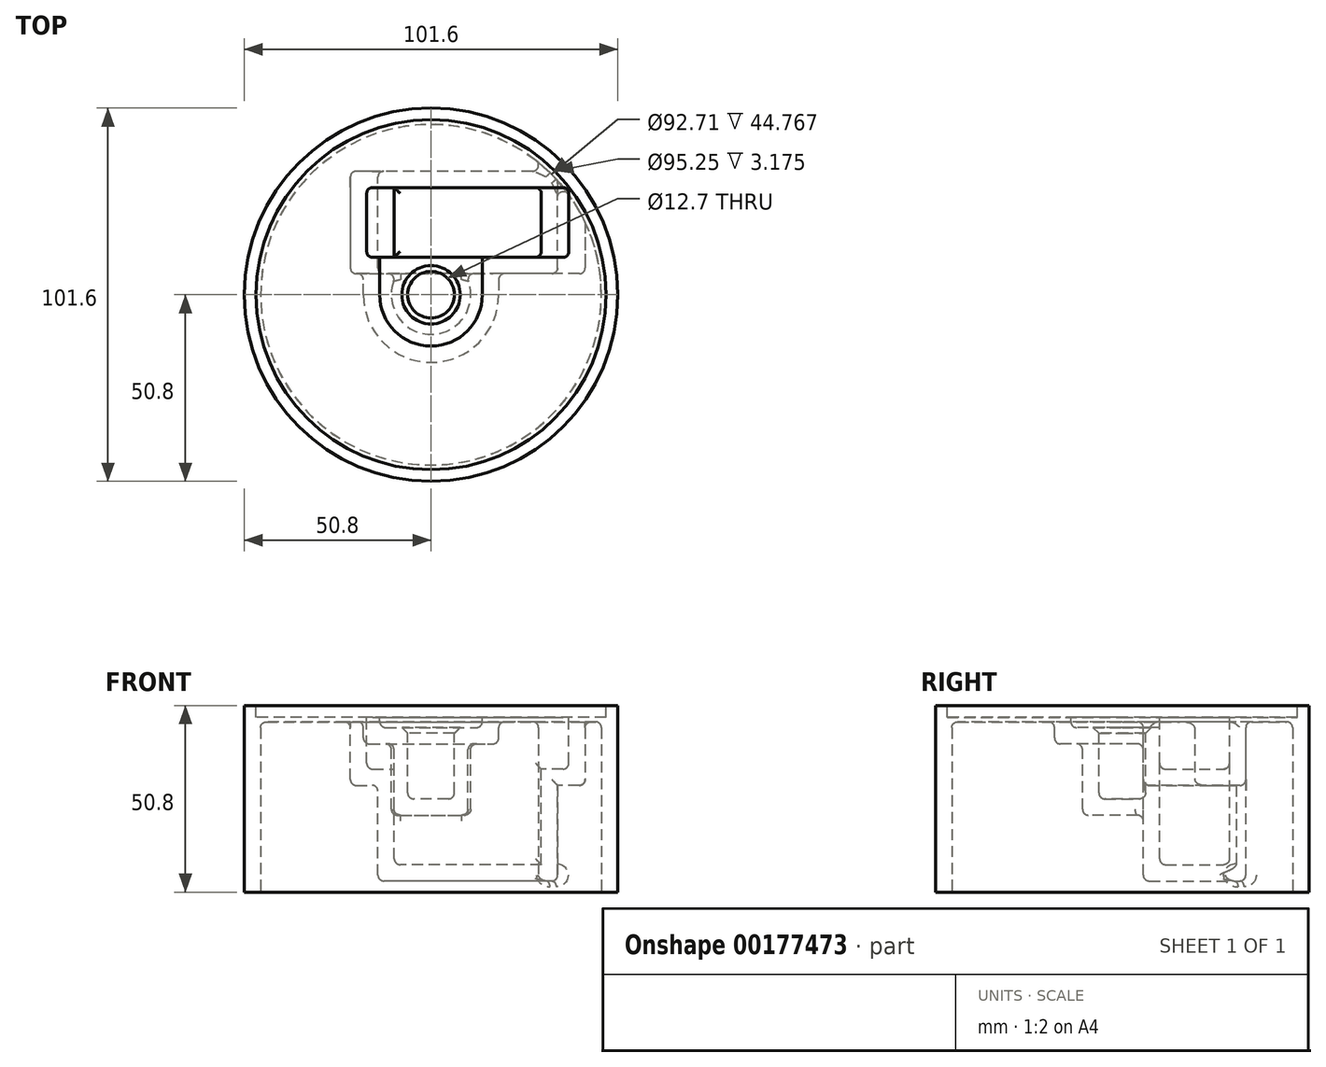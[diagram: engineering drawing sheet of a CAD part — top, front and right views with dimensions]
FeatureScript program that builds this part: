
annotation { "Feature Type Name" : "Feature", "Feature Type Description" : "" }
export const myFeature = defineFeature(function(context is Context, id is Id, definition is map)
    precondition{}
    {
        {
            var Q0;
            Q0=qCreatedBy(makeId("Top.planeOp"),FACE);
            var sketch = newSketch(context, id + "F0", { "sketchPlane" : qUnion([Q0])});
            skCircle(sketch, "E0", {"center": v(0, 0) * mm, "radius": 50.8 * mm});
            skSolve(sketch);
        }
        {
            var Q0;
            Q0 = qSketchRegion(id + "F0", true);
            extrude(context, id + "F1", {"entities" : qUnion([Q0]), "depth" : 50.8 * mm});
        }
        {
            var Q0;
            Q0=makeQuery(id+"F1.opExtrude","CAP_FACE",FACE,{"disambiguationData":[OSD([sQuery(id+"F0.wireOp",EDGE,"E0")])],"isStart":false});
            var sketch = newSketch(context, id + "F2", { "sketchPlane" : qUnion([Q0])});
            skCircle(sketch, "E1", {"center": v(0, 0) * mm, "radius": 13.02 * mm});
            skCircle(sketch, "E2", {"center": v(0, 19.69) * mm, "radius": 6.67 * mm});
            skLineSegment(sketch, "E3", {"start": v(-24.88, 13.98) * mm, "end": v(-19.78, -16.5) * mm});
            skLineSegment(sketch, "E4", {"start": v(-19.78, -16.5) * mm, "end": v(3.2, -22.09) * mm});
            skLineSegment(sketch, "E5", {"start": v(3.2, -22.09) * mm, "end": v(-19.1, -28.35) * mm});
            skLineSegment(sketch, "E6", {"start": v(-19.1, -28.35) * mm, "end": v(-34.98, -6.69) * mm});
            skLineSegment(sketch, "E7", {"start": v(-34.98, -6.69) * mm, "end": v(-24.88, 13.98) * mm});
            skSolve(sketch);
        }
        {
            var Q0;
            Q0=makeQuery(id+"F2.imprint","IMPRINT",FACE,{"disambiguationData":[TD([[makeQuery(id+"F2.imprint","IMPRINT",EDGE,{"derivedFrom":sQuery(id+"F2.wireOp",EDGE,"E1")}),-1.0]])]});
            var sketch = newSketch(context, id + "F3", { "sketchPlane" : qUnion([Q0])});
            skLineSegment(sketch, "E8.bottom", {"start": v(30, 10.19) * mm, "end": v(-10, 10.18) * mm});
            skLineSegment(sketch, "E8.top", {"start": v(30, 29.19) * mm, "end": v(-10, 29.18) * mm});
            skLineSegment(sketch, "E8.left", {"start": v(30, 10.19) * mm, "end": v(30, 29.19) * mm});
            skLineSegment(sketch, "E8.right", {"start": v(-10, 10.18) * mm, "end": v(-10, 29.18) * mm});
            skPoint(sketch, "E8.middle", {"position": v(10, 19.69) * mm});
            skSolve(sketch);
        }
        {
            var Q0;
            Q0 = qSketchRegion(id + "F3", true);
            extrude(context, id + "F4", {"entities" : qUnion([Q0]), "operationType" : NewBodyOperationType.REMOVE, "oppositeDirection" : true, "depth" : 43.3 * mm});
        }
        {
            var Q0;
            Q0=makeQuery(id+"F2.imprint","IMPRINT",FACE,{"disambiguationData":[TD([[makeQuery(id+"F2.imprint","IMPRINT",EDGE,{"derivedFrom":sQuery(id+"F2.wireOp",EDGE,"E1")}),-1.0]])]});
            var sketch = newSketch(context, id + "F5", { "sketchPlane" : qUnion([Q0])});
            skLineSegment(sketch, "E9.0", {"start": v(-10, 10.18) * mm, "end": v(-10, 29.18) * mm});
            skLineSegment(sketch, "E9.1", {"start": v(30, 10.19) * mm, "end": v(30, 29.19) * mm});
            skLineSegment(sketch, "E10", {"start": v(-10, 29.18) * mm, "end": v(-17.5, 29.18) * mm});
            skLineSegment(sketch, "E11", {"start": v(-17.5, 29.18) * mm, "end": v(-17.5, 10.18) * mm});
            skLineSegment(sketch, "E12", {"start": v(-17.5, 10.18) * mm, "end": v(-10, 10.18) * mm});
            skLineSegment(sketch, "E13", {"start": v(30, 29.18) * mm, "end": v(37.5, 29.18) * mm});
            skLineSegment(sketch, "E14", {"start": v(37.5, 29.19) * mm, "end": v(37.5, 10.18) * mm});
            skLineSegment(sketch, "E15", {"start": v(37.5, 10.18) * mm, "end": v(30, 10.18) * mm});
            skSolve(sketch);
        }
        {
            var Q0;
            Q0 = qSketchRegion(id + "F5", true);
            extrude(context, id + "F6", {"entities" : qUnion([Q0]), "operationType" : NewBodyOperationType.REMOVE, "oppositeDirection" : true, "depth" : (43.3 - 26) * mm});
        }
        {
            var Q0;
            Q0=makeQuery(id+"F2.imprint","IMPRINT",FACE,{"disambiguationData":[TD([[makeQuery(id+"F2.imprint","IMPRINT",EDGE,{"derivedFrom":sQuery(id+"F2.wireOp",EDGE,"E1")}),-1.0]])]});
            var sketch = newSketch(context, id + "F7", { "sketchPlane" : qUnion([Q0])});
            skArc(sketch, "E16", {"start": v(-13.97, 0) * mm, "mid": v(0, -13.97) * mm, "end": v(13.97, 0) * mm});
            skLineSegment(sketch, "E17", {"start": v(-13.97, 0) * mm, "end": v(-13.97, 10.18) * mm});
            skLineSegment(sketch, "E18", {"start": v(-13.97, 10.18) * mm, "end": v(13.97, 10.18) * mm});
            skLineSegment(sketch, "E19", {"start": v(13.97, 10.18) * mm, "end": v(13.97, 0) * mm});
            skSolve(sketch);
        }
        {
            var Q0;
            Q0 = qSketchRegion(id + "F7", true);
            var Q1;
            Q1=makeQuery(id+"F6.boolean.opBoolean","COPY",FACE,{"derivedFrom":makeQuery(id+"F6.opExtrude","CAP_FACE",FACE,{"disambiguationData":[OSD([sQuery(id+"F5.wireOp",EDGE,"E9.0"),sQuery(id+"F5.wireOp",EDGE,"E10"),sQuery(id+"F5.wireOp",EDGE,"E11"),sQuery(id+"F5.wireOp",EDGE,"E12")])],"isStart":false})});
            extrude(context, id + "F8", {"entities" : qUnion([Q0]), "operationType" : NewBodyOperationType.REMOVE, "oppositeDirection" : true, "endBoundEntityFace" : qUnion([Q1]), "depth" : 6 * mm});
        }
        {
            var Q0;
            Q0=makeQuery(id+"F2.imprint","IMPRINT",FACE,{"disambiguationData":[TD([[makeQuery(id+"F2.imprint","IMPRINT",EDGE,{"derivedFrom":sQuery(id+"F2.wireOp",EDGE,"E1")}),1.0]])]});
            var sketch = newSketch(context, id + "F9", { "sketchPlane" : qUnion([Q0])});
            skCircle(sketch, "E20", {"center": v(0, 0) * mm, "radius": 6.35 * mm});
            skSolve(sketch);
        }
        {
            var Q0;
            Q0 = qSketchRegion(id + "F9", true);
            extrude(context, id + "F10", {"entities" : qUnion([Q0]), "operationType" : NewBodyOperationType.REMOVE, "oppositeDirection" : true, "depth" : 25.4 * mm});
        }
        {
            var Q0;
            Q0=makeQuery(id+"F1.opExtrude","CAP_FACE",FACE,{"disambiguationData":[OSD([sQuery(id+"F0.wireOp",EDGE,"E0")])],"isStart":true});
            shell(context, id + "F11", {"entities" : qUnion([Q0]), "thickness" : 4.44 * mm});
        }
        {
            var Q0;
            Q0=makeQuery(id+"F2.imprint","IMPRINT",FACE,{"disambiguationData":[TD([[makeQuery(id+"F2.imprint","IMPRINT",EDGE,{"derivedFrom":sQuery(id+"F2.wireOp",EDGE,"E1")}),-1.0]])]});
            var sketch = newSketch(context, id + "F12", { "sketchPlane" : qUnion([Q0])});
            skCircle(sketch, "E21", {"center": v(0, 0) * mm, "radius": 47.62 * mm});
            skSolve(sketch);
        }
        {
            var Q0;
            Q0 = qSketchRegion(id + "F12", true);
            extrude(context, id + "F13", {"entities" : qUnion([Q0]), "operationType" : NewBodyOperationType.REMOVE, "oppositeDirection" : true, "depth" : 3.17 * mm});
        }
        {
            var Q0;
            Q0=makeQuery(id+"F8.boolean.opBoolean","COPY",EDGE,{"derivedFrom":makeQuery(id+"F8.opExtrude","CAP_EDGE",EDGE,{"disambiguationData":[OSD([sQuery(id+"F7.wireOp",EDGE,"E17")])],"isStart":false})});
            var Q1;
            Q1=makeQuery(id+"F6.boolean.opBoolean","COPY",EDGE,{"derivedFrom":makeQuery(id+"F6.opExtrude","CAP_EDGE",EDGE,{"disambiguationData":[OSD([sQuery(id+"F5.wireOp",EDGE,"E11")])],"isStart":false})});
            var Q2;
            Q2=makeQuery(id+"F6.boolean.opBoolean","COPY",EDGE,{"derivedFrom":makeQuery(id+"F6.opExtrude","CAP_EDGE",EDGE,{"disambiguationData":[OSD([sQuery(id+"F5.wireOp",EDGE,"E10")])],"isStart":false})});
            var Q3;
            Q3=makeQuery(id+"F6.boolean.opBoolean","COPY",EDGE,{"derivedFrom":makeQuery(id+"F6.opExtrude","CAP_EDGE",EDGE,{"disambiguationData":[OSD([sQuery(id+"F5.wireOp",EDGE,"E9.0")])],"isStart":false})});
            var Q4;
            Q4=makeQuery(id+"F4.boolean.opBoolean","COPY",EDGE,{"derivedFrom":makeQuery(id+"F4.opExtrude","CAP_EDGE",EDGE,{"disambiguationData":[OSD([sQuery(id+"F3.wireOp",EDGE,"E8.right")])],"isStart":false})});
            var Q5;
            Q5=makeQuery(id+"F4.boolean.opBoolean","COPY",EDGE,{"derivedFrom":makeQuery(id+"F4.opExtrude","CAP_EDGE",EDGE,{"disambiguationData":[OSD([sQuery(id+"F3.wireOp",EDGE,"E8.top")])],"isStart":false})});
            var Q6;
            Q6=makeQuery(id+"F6.boolean.opBoolean","COPY",EDGE,{"derivedFrom":makeQuery(id+"F6.opExtrude","SWEPT_EDGE",EDGE,{"disambiguationData":[OSD([sQuery(id+"F5.wireOp",EDGE,"E11"),sQuery(id+"F5.wireOp",EDGE,"E12")])]})});
            var Q7;
            Q7=makeQuery(id+"F6.boolean.opBoolean","COPY",EDGE,{"derivedFrom":makeQuery(id+"F6.opExtrude","CAP_EDGE",EDGE,{"disambiguationData":[OSD([sQuery(id+"F5.wireOp",EDGE,"E12")])],"isStart":false})});
            var Q8;
            Q8=makeQuery(id+"F4.boolean.opBoolean","COPY",EDGE,{"derivedFrom":makeQuery(id+"F4.opExtrude","CAP_EDGE",EDGE,{"disambiguationData":[OSD([sQuery(id+"F3.wireOp",EDGE,"E8.bottom")])],"isStart":false})});
            var Q9;
            Q9=makeQuery(id+"F4.boolean.opBoolean","COPY",EDGE,{"derivedFrom":makeQuery(id+"F4.opExtrude","SWEPT_EDGE",EDGE,{"disambiguationData":[OSD([sQuery(id+"F3.wireOp",EDGE,"E8.bottom"),sQuery(id+"F3.wireOp",EDGE,"E8.left")])]})});
            var Q10;
            Q10=makeQuery(id+"F4.boolean.opBoolean","COPY",EDGE,{"derivedFrom":makeQuery(id+"F4.opExtrude","SWEPT_EDGE",EDGE,{"disambiguationData":[OSD([sQuery(id+"F3.wireOp",EDGE,"E8.top"),sQuery(id+"F3.wireOp",EDGE,"E8.left")])]})});
            var Q11;
            Q11=makeQuery(id+"F6.boolean.opBoolean","COPY",EDGE,{"derivedFrom":makeQuery(id+"F6.opExtrude","CAP_EDGE",EDGE,{"disambiguationData":[OSD([sQuery(id+"F5.wireOp",EDGE,"E13")])],"isStart":false})});
            var Q12;
            Q12=makeQuery(id+"F6.boolean.opBoolean","COPY",EDGE,{"derivedFrom":makeQuery(id+"F6.opExtrude","SWEPT_EDGE",EDGE,{"disambiguationData":[OSD([sQuery(id+"F5.wireOp",EDGE,"E13"),sQuery(id+"F5.wireOp",EDGE,"E14")])]})});
            var Q13;
            Q13=makeQuery(id+"F6.boolean.opBoolean","COPY",EDGE,{"derivedFrom":makeQuery(id+"F6.opExtrude","SWEPT_EDGE",EDGE,{"disambiguationData":[OSD([sQuery(id+"F5.wireOp",EDGE,"E14"),sQuery(id+"F5.wireOp",EDGE,"E15")])]})});
            var Q14;
            Q14=makeQuery(id+"F6.boolean.opBoolean","COPY",EDGE,{"derivedFrom":makeQuery(id+"F6.opExtrude","CAP_EDGE",EDGE,{"disambiguationData":[OSD([sQuery(id+"F5.wireOp",EDGE,"E14")])],"isStart":false})});
            var Q15;
            Q15=makeQuery(id+"F6.boolean.opBoolean","COPY",EDGE,{"derivedFrom":makeQuery(id+"F6.opExtrude","CAP_EDGE",EDGE,{"disambiguationData":[OSD([sQuery(id+"F5.wireOp",EDGE,"E15")])],"isStart":false})});
            var Q16;
            Q16=makeQuery(id+"F6.boolean.opBoolean","COPY",EDGE,{"derivedFrom":makeQuery(id+"F6.opExtrude","CAP_EDGE",EDGE,{"disambiguationData":[OSD([sQuery(id+"F5.wireOp",EDGE,"E9.1")])],"isStart":false})});
            var Q17;
            Q17=makeQuery(id+"F8.boolean.opBoolean","COPY",EDGE,{"derivedFrom":makeQuery(id+"F8.opExtrude","SWEPT_EDGE",EDGE,{"disambiguationData":[OSD([sQuery(id+"F7.wireOp",EDGE,"E17"),sQuery(id+"F7.wireOp",EDGE,"E18")])]})});
            var Q18;
            {var subQ0=sQuery(id+"F0.wireOp",EDGE,"E0");Q18=makeQuery(id+"F11.opShell","OFFSET_EDGE",EDGE,{"disambiguationData":[OSD([subQ0]),TDD([makeQuery(id+"F1.opExtrude","CAP_EDGE",EDGE,{"disambiguationData":[OSD([subQ0])],"isStart":false})])]});}
            var Q19;
            Q19=makeQuery(id+"F6.boolean.opBoolean","COPY",EDGE,{"derivedFrom":makeQuery(id+"F6.opExtrude","SWEPT_EDGE",EDGE,{"disambiguationData":[OSD([sQuery(id+"F5.wireOp",EDGE,"E10"),sQuery(id+"F5.wireOp",EDGE,"E11")])]})});
            var Q20;
            Q20=makeQuery(id+"F11.opShell","OFFSET_FACE",FACE,{"disambiguationData":[OSD([sQuery(id+"F3.wireOp",EDGE,"E8.bottom"),sQuery(id+"F3.wireOp",EDGE,"E8.top"),sQuery(id+"F3.wireOp",EDGE,"E8.left"),sQuery(id+"F3.wireOp",EDGE,"E8.right")])]});
            var Q21;
            Q21=makeQuery(id+"F11.opShell","OFFSET_FACE",FACE,{"disambiguationData":[OSD([sQuery(id+"F3.wireOp",EDGE,"E8.bottom"),sQuery(id+"F5.wireOp",EDGE,"E12"),sQuery(id+"F5.wireOp",EDGE,"E15")])]});
            var Q22;
            Q22=makeQuery(id+"F11.opShell","OFFSET_FACE",FACE,{"disambiguationData":[OSD([sQuery(id+"F3.wireOp",EDGE,"E8.right")])]});
            var Q23;
            Q23=makeQuery(id+"F11.opShell","OFFSET_FACE",FACE,{"disambiguationData":[OSD([sQuery(id+"F3.wireOp",EDGE,"E8.top"),sQuery(id+"F5.wireOp",EDGE,"E10"),sQuery(id+"F5.wireOp",EDGE,"E13")])]});
            var Q24;
            {var subQ0=sQuery(id+"F5.wireOp",EDGE,"E11");Q24=makeQuery(id+"F11.opShell","OFFSET_EDGE",EDGE,{"disambiguationData":[OSD([subQ0]),TDD([makeQuery(id+"F6.boolean.opBoolean","COPY",EDGE,{"derivedFrom":makeQuery(id+"F6.opExtrude","CAP_EDGE",EDGE,{"disambiguationData":[OSD([subQ0])],"isStart":false})})])]});}
            var Q25;
            {var subQ0=sQuery(id+"F9.wireOp",EDGE,"E20");Q25=makeQuery(id+"F11.opShell","OFFSET_FACE",FACE,{"disambiguationData":[OSD([subQ0]),TDD([makeQuery(id+"F10.boolean.opBoolean","COPY",FACE,{"derivedFrom":makeQuery(id+"F10.opExtrude","SWEPT_FACE",FACE,{"disambiguationData":[OSD([subQ0])]})})])]});}
            var Q26;
            Q26=makeQuery(id+"F11.opShell","OFFSET_FACE",FACE,{"disambiguationData":[OSD([sQuery(id+"F7.wireOp",EDGE,"E16")])]});
            var Q27;
            {var subQ0=sQuery(id+"F5.wireOp",EDGE,"E14");Q27=makeQuery(id+"F11.opShell","OFFSET_EDGE",EDGE,{"disambiguationData":[OSD([subQ0]),TDD([makeQuery(id+"F6.boolean.opBoolean","COPY",EDGE,{"derivedFrom":makeQuery(id+"F6.opExtrude","CAP_EDGE",EDGE,{"disambiguationData":[OSD([subQ0])],"isStart":false})})])]});}
            var Q28;
            Q28=makeQuery(id+"F10.boolean.opBoolean","COPY",EDGE,{"derivedFrom":makeQuery(id+"F10.opExtrude","CAP_EDGE",EDGE,{"disambiguationData":[OSD([sQuery(id+"F9.wireOp",EDGE,"E20")])],"isStart":false})});
            fillet(context, id + "F14", {"entities" : qUnion([Q0, Q1, Q2, Q3, Q4, Q5, Q6, Q7, Q8, Q9, Q10, Q11, Q12, Q13, Q14, Q15, Q16, Q17, Q18, Q19, Q20, Q21, Q22, Q23, Q24, Q25, Q26, Q27, Q28]), "radius" : 1.59 * mm, "tangentPropagation" : true, "allowEdgeOverflow" : false});
        }
        {
            var Q0;
            Q0=makeQuery(id+"F10.boolean.opBoolean","INTERSECT",EDGE,{"derivedFrom":[makeQuery(id+"F8.boolean.opBoolean","COPY",FACE,{"derivedFrom":makeQuery(id+"F8.opExtrude","CAP_FACE",FACE,{"disambiguationData":[OSD([sQuery(id+"F7.wireOp",EDGE,"E16"),sQuery(id+"F7.wireOp",EDGE,"E17"),sQuery(id+"F7.wireOp",EDGE,"E18"),sQuery(id+"F7.wireOp",EDGE,"E19")])],"isStart":false})}),makeQuery(id+"F10.opExtrude","SWEPT_FACE",FACE,{"disambiguationData":[OSD([sQuery(id+"F9.wireOp",EDGE,"E20")])]})]});
            chamfer(context, id + "F15", {"entities" : qUnion([Q0]), "width" : 1.59 * mm, "tangentPropagation" : true});
        }
    });
